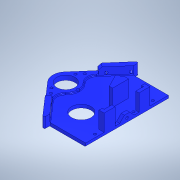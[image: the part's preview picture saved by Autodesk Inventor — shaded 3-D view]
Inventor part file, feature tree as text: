
AUTODESK INVENTOR PART (.ipt)
format: ipt  version: 2022 (Build 260153000, 153)  size: 486,400 bytes
history: native  units: in
note: dims shown in document units (in); Inventor stores cm internally (conversion verified against a paired STEP export)
features: sketch x14, extrude x10, reference x9, projected_geometry x6, other x6, hole x4, fillet x2, chamfer x2, mirror x1, revolve x1, pattern_circular x1
ambient origin geometry x8: Origin, YZ Plane, XZ Plane, XY Plane, X Axis, Y Axis, Z Axis, Center Point
bodies: Solid3 (feature_tree)
feature tree (56):
  extrude  "Extrusion13"  Depth=2.1654in
  extrude  "Extrusion14"  Depth=1.7717in TaperAngle=0.0deg
  mirror  "Mirror4"
  extrude  "Extrusion25"  Depth=0.1969in TaperAngle=0.0deg
  extrude  "Extrusion26"  Depth=1.5748in
  extrude  "Extrusion28"  Depth=1.1024in
  extrude  "Extrusion35"  Depth=0.5906in
  extrude  "Extrusion38"  Depth=1.1024in
  extrude  "Extrusion39"  TaperAngle=0.0deg  [1 undecoded]
  hole  "Hole5"  [1 undecoded]
  fillet  "Fillet3"  [1 undecoded]
  fillet  "Fillet4"  Radius=1.5354in
  hole  "Hole6"  [1 undecoded]
  hole  "Hole7"  [1 undecoded]
  chamfer  "Chamfer3"  Distance=0.3937in
  chamfer  "Chamfer4"  Distance=0.3937in
  extrude  "Extrusion40"  Depth=0.9055in
  hole  "Hole8"  [1 undecoded]
  extrude  "Extrusion41"  Depth=0.1969in
  revolve  "Revolution1"  [1 undecoded]
  pattern_circular  "Circular Pattern1"  Count=3  [1 undecoded]
  sketch  "Sketch14"  dims[d94=0.9646in d95=2.1654in]
  sketch  "Sketch15"  dims[d96=1.7717in d97=0.4433in d98=0.0in]
  projected_geometry  "Projected Loop7"
  sketch  "Sketch26"  dims[d99=2.5561in d100=0.1969in d101=0.0in]
  sketch  "Sketch29"  dims[d137=0.7874in d138=1.5748in]
  sketch  "Sketch37"  dims[d139=0.1969in d140=0.0in d141=1.1024in]
  projected_geometry  "Projected Loop19"
  sketch  "Sketch40"  dims[d143=0.0787in d144=0.0in d145=0.5906in]
  projected_geometry  "Projected Loop20"
  sketch  "Sketch41"  dims[d146=1.1024in d151=1.1811in]
  projected_geometry  "Projected Loop21"
  sketch  "Sketch42"  dims[d152=0.3937in d153=0.0in d185=0.0in d186=0.0in]
  projected_geometry  "Projected Loop22"
  sketch  "Sketch43"  dims[d198=0.4724in d199=0.4724in d200=0.0in d201=0.0in d202=1.5354in]
  reference  "Reference1"
  reference  "Reference2"
  sketch  "Sketch44"  dims[d203=1.7717in d204=1.8504in]
  reference  "Reference3"
  reference  "Reference4"
  sketch  "Sketch45"  dims[d205=0.3937in d206=0.0in d207=1.8504in]
  sketch  "Sketch46"  dims[d208=0.3937in]
  reference  "Reference5"
  sketch  "Sketch47"  dims[d209=0.3937in]
  reference  "Reference6"
  reference  "Reference7"
  projected_geometry  "Projected Loop23"
  reference  "Reference8"
  reference  "Reference9"
  sketch  "Sketch49"  dims[d210=0.9449in d211=0.3937in d213=0.3937in d214=0.9055in d215=0.9055in d216=0.1969in d217=0.1969in d220=1.1811in d221=1.1811in d222=1.1811in d223=0.7553in d224=0.7553in d225=1.1811in d226=0.1575in d227=0.2362in d228=0.248in d229=0.0787in d230=90.0deg d231=0.2756in d232=0.0in d233=0.0787in d234=0.0394in d235=0.1575in d236=0.2362in d237=0.1575in d238=0.0787in d239=90.0deg d240=0.315in d241=0.8108in d242=0.1575in d243=0.2362in d244=0.1575in d245=0.0787in d246=90.0deg d247=0.315in d248=0.8108in d249=0.0394in d250=0.0787in d251=45.0deg d252=0.1575in d253=0.0787in d254=45.0deg d255=0.2913in d256=0.315in d257=135.0deg d258=0.1969in d259=0.0in d260=0.1575in d261=0.2362in d262=0.1575in d263=0.0787in d264=90.0deg d265=0.315in d266=0.0in d268=0.1417in d269=0.1417in d270=0.9843in d271=0.1969in d273=0.1417in d274=0.1417in d275=0.3937in d276=0.0in d277=0.1181in d278=0.1969in d279=0.1969in d280=0.1181in d289=0.3937in d290=0.5906in d291=15.0deg d292=0.7874in d293=360.0deg d93=0.1575in d107=0.0197in d108=0.0344in d109=0.0197in d110=0.0344in d154=0.0197in d155=0.0344in d294=0.0344in]
  parser-record x1  (decoder bookkeeping rows leaked as tree rows — omitted from the tree; the rows remain in map.json)
  other  "Main Body.iam"
  other  "Front Armor:2"
  other  "Front Armor:1"
  other  "Base Plate:2"
  other  "Battery:1"
note: 8 required parameter values undecoded (feature->parameter linkage not recoverable at this tier; creation-order binding heuristic only, values carry confidence <= 0.55)
note: 1 file-system path scrubbed to <path> (originals preserved in map.json)